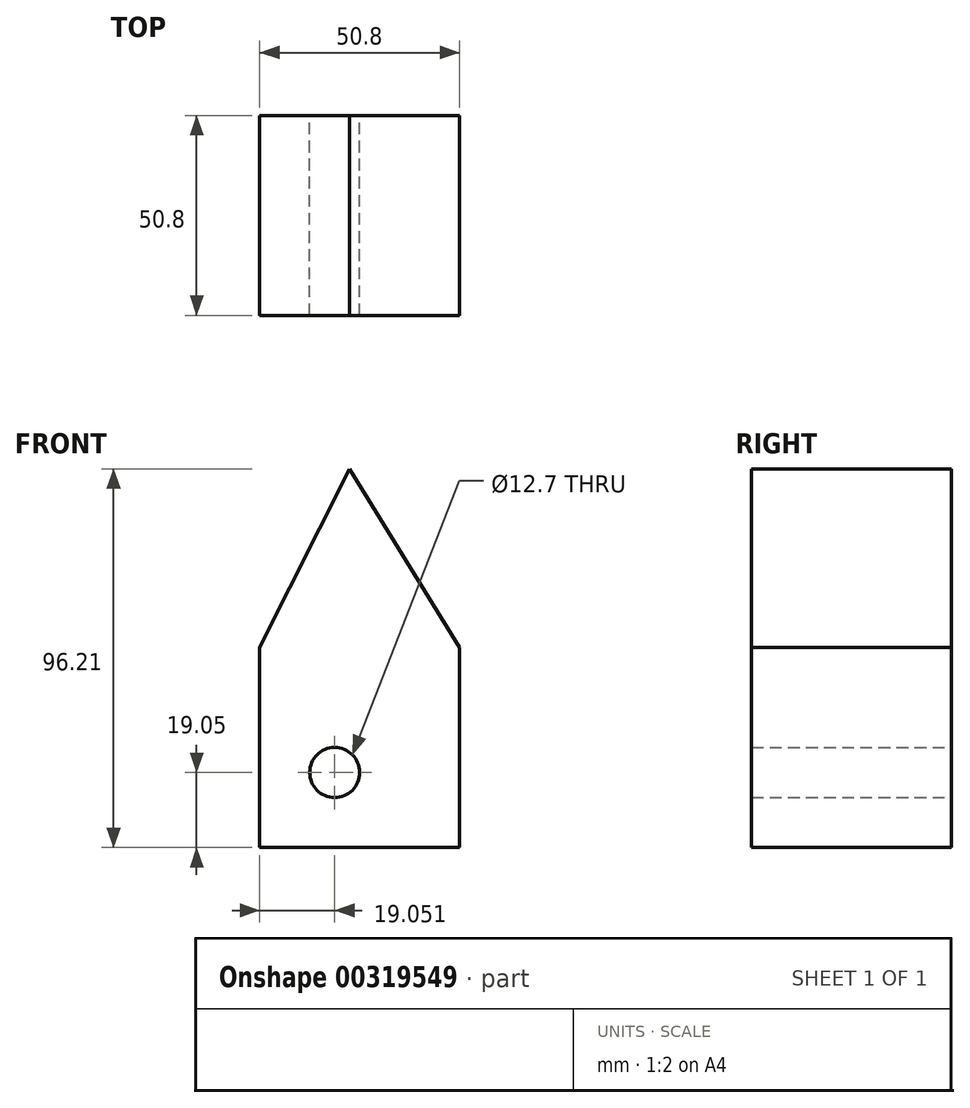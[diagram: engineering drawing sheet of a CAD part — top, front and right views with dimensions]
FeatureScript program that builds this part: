
annotation { "Feature Type Name" : "Feature", "Feature Type Description" : "" }
export const myFeature = defineFeature(function(context is Context, id is Id, definition is map)
    precondition{}
    {
        {
            var Q0;
            Q0=qCreatedBy(makeId("Front.planeOp"),FACE);
            var sketch = newSketch(context, id + "F0", { "sketchPlane" : qUnion([Q0])});
            skLineSegment(sketch, "E0.bottom", {"start": v(7.74, 3.75) * mm, "end": v(58.54, 3.75) * mm});
            skLineSegment(sketch, "E0.top", {"start": v(7.74, -47.05) * mm, "end": v(58.54, -47.05) * mm});
            skLineSegment(sketch, "E0.left", {"start": v(7.74, 3.75) * mm, "end": v(7.74, -47.05) * mm});
            skLineSegment(sketch, "E0.right", {"start": v(58.54, 3.75) * mm, "end": v(58.54, -47.05) * mm});
            skLineSegment(sketch, "E1", {"start": v(7.74, 3.75) * mm, "end": v(30.5, 49.16) * mm});
            skLineSegment(sketch, "E2", {"start": v(58.54, 3.75) * mm, "end": v(30.5, 49.16) * mm});
            skLineSegment(sketch, "E3.0", {"start": v(26.8, 3.75) * mm, "end": v(26.8, -47.05) * mm});
            skLineSegment(sketch, "E4.0", {"start": v(7.74, -28) * mm, "end": v(58.54, -28) * mm});
            skCircle(sketch, "E5", {"center": v(26.8, -28) * mm, "radius": 6.35 * mm});
            skSolve(sketch);
        }
        {
            var Q0;
            {var subQ5=sQuery(id+"F0.wireOp",EDGE,"E0.bottom");var subQ7=sQuery(id+"F0.wireOp",EDGE,"E3.0");var subQ8=makeQuery(id+"F0.imprint","INTERSECT",VERTEX,{"derivedFrom":[subQ5,subQ7]});Q0=makeQuery(id+"F0.imprint","IMPRINT",FACE,{"disambiguationData":[TD([[makeQuery(id+"F0.imprint","IMPRINT",EDGE,{"disambiguationData":[TD([[subQ8,-1.0]])],"derivedFrom":subQ7}),1.0]])]});}
            var Q1;
            {var subQ5=sQuery(id+"F0.wireOp",EDGE,"E0.bottom");var subQ7=sQuery(id+"F0.wireOp",EDGE,"E3.0");var subQ8=makeQuery(id+"F0.imprint","INTERSECT",VERTEX,{"derivedFrom":[subQ5,subQ7]});Q1=makeQuery(id+"F0.imprint","IMPRINT",FACE,{"disambiguationData":[TD([[makeQuery(id+"F0.imprint","IMPRINT",EDGE,{"disambiguationData":[TD([[subQ8,-1.0]])],"derivedFrom":subQ7}),-1.0]])]});}
            var Q2;
            {var subQ1=sQuery(id+"F0.wireOp",EDGE,"E0.left");var subQ6=sQuery(id+"F0.wireOp",EDGE,"E0.top");var subQ9=makeQuery(id+"F0.imprint","INTERSECT",VERTEX,{"derivedFrom":[subQ6,subQ1]});Q2=makeQuery(id+"F0.imprint","IMPRINT",FACE,{"disambiguationData":[TD([[makeQuery(id+"F0.imprint","IMPRINT",EDGE,{"disambiguationData":[TD([[subQ9,-1.0]])],"derivedFrom":subQ6}),1.0]])]});}
            var Q3;
            {var subQ1=sQuery(id+"F0.wireOp",EDGE,"E0.right");var subQ5=sQuery(id+"F0.wireOp",EDGE,"E0.top");var subQ6=makeQuery(id+"F0.imprint","INTERSECT",VERTEX,{"derivedFrom":[subQ5,subQ1]});Q3=makeQuery(id+"F0.imprint","IMPRINT",FACE,{"disambiguationData":[TD([[makeQuery(id+"F0.imprint","IMPRINT",EDGE,{"disambiguationData":[TD([[subQ6,1.0]])],"derivedFrom":subQ5}),1.0]])]});}
            var Q4;
            {var subQ0=sQuery(id+"F0.wireOp",EDGE,"E1");Q4=makeQuery(id+"F0.imprint","IMPRINT",FACE,{"disambiguationData":[TD([[makeQuery(id+"F0.imprint","IMPRINT",EDGE,{"derivedFrom":subQ0}),-1.0]])]});}
            extrude(context, id + "F1", {"entities" : qUnion([Q0, Q1, Q2, Q3, Q4]), "depth" : 50.8 * mm});
        }
    });
